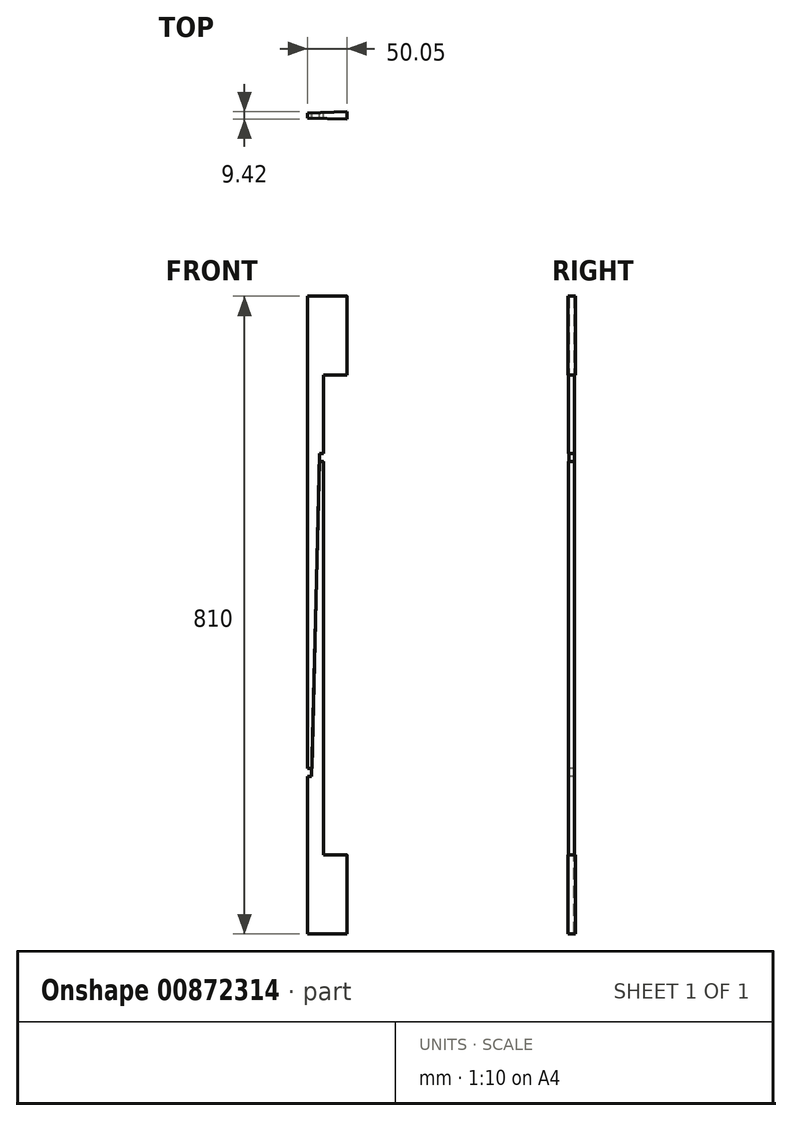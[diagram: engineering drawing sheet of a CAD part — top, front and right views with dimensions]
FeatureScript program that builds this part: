
annotation { "Feature Type Name" : "Feature", "Feature Type Description" : "" }
export const myFeature = defineFeature(function(context is Context, id is Id, definition is map)
    precondition{}
    {
        {
            var Q0;
            Q0=qCreatedBy(makeId("Front.planeOp"),FACE);
            var sketch = newSketch(context, id + "F0", { "sketchPlane" : qUnion([Q0])});
            skLineSegment(sketch, "E0", {"start": v(0, 0) * mm, "end": v(0, 810) * mm, "construction": true});
            skLineSegment(sketch, "E1", {"start": v(100, 0) * mm, "end": v(100, 200) * mm});
            skLineSegment(sketch, "E2", {"start": v(100, 200) * mm, "end": v(105, 200) * mm});
            skLineSegment(sketch, "E3", {"start": v(105, 200) * mm, "end": v(115, 600) * mm});
            skLineSegment(sketch, "E4", {"start": v(115, 600) * mm, "end": v(120, 600) * mm});
            skLineSegment(sketch, "E5", {"start": v(120, 600) * mm, "end": v(120, 100) * mm});
            skLineSegment(sketch, "E6", {"start": v(120, 100) * mm, "end": v(150, 100) * mm});
            skLineSegment(sketch, "E7", {"start": v(150, 100) * mm, "end": v(150, 0) * mm});
            skLineSegment(sketch, "E8", {"start": v(150, 0) * mm, "end": v(100, 0) * mm});
            skLineSegment(sketch, "E9", {"start": v(100, 210) * mm, "end": v(105.25, 210) * mm});
            skLineSegment(sketch, "E10", {"start": v(105.25, 210) * mm, "end": v(115.25, 610) * mm});
            skLineSegment(sketch, "E11", {"start": v(115.25, 610) * mm, "end": v(120, 610) * mm});
            skLineSegment(sketch, "E12", {"start": v(120, 610) * mm, "end": v(120, 710) * mm});
            skLineSegment(sketch, "E13", {"start": v(120, 710) * mm, "end": v(150, 710) * mm});
            skLineSegment(sketch, "E14", {"start": v(150, 710) * mm, "end": v(150, 810) * mm});
            skLineSegment(sketch, "E15", {"start": v(150, 810) * mm, "end": v(100, 810) * mm});
            skLineSegment(sketch, "E16", {"start": v(100, 810) * mm, "end": v(100, 210) * mm});
            skSolve(sketch);
        }
        {
            var Q0;
            {var subQ3=sQuery(id+"F0.wireOp",EDGE,"E9");Q0=makeQuery(id+"F0.imprint","IMPRINT",FACE,{"disambiguationData":[TD([[makeQuery(id+"F0.imprint","IMPRINT",EDGE,{"derivedFrom":subQ3}),1.0]])]});}
            var Q1;
            Q1=sQuery(id+"F0.wireOp",EDGE,"E0");
            revolve(context, id + "F1", {"surfaceOperationType" : NewSurfaceOperationType.NEW, "entities" : qUnion([Q0]), "axis" : qUnion([Q1]), "revolveType" : RevolveType.SYMMETRIC, "angle" : 3.6 * degree});
        }
        {
            var Q0;
            Q0=makeQuery(id+"F0.imprint","IMPRINT",FACE,{"disambiguationData":[TD([[makeQuery(id+"F0.imprint","IMPRINT",EDGE,{"derivedFrom":sQuery(id+"F0.wireOp",EDGE,"E1")}),-1.0]])]});
            var Q1;
            Q1=sQuery(id+"F0.wireOp",EDGE,"E0");
            revolve(context, id + "F2", {"surfaceOperationType" : NewSurfaceOperationType.NEW, "entities" : qUnion([Q0]), "axis" : qUnion([Q1]), "revolveType" : RevolveType.SYMMETRIC, "angle" : 3.6 * degree});
        }
    });
